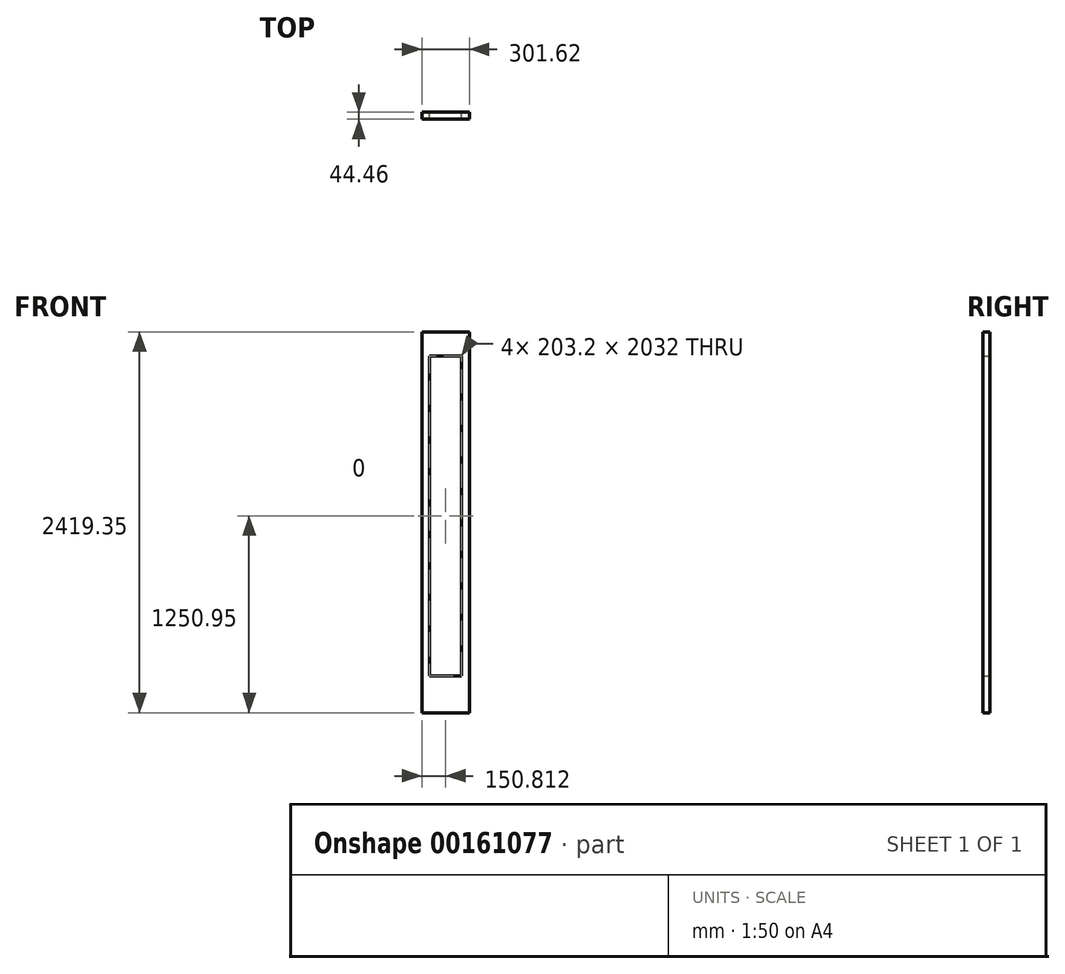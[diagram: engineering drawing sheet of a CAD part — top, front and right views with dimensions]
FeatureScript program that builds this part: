
annotation { "Feature Type Name" : "Feature", "Feature Type Description" : "" }
export const myFeature = defineFeature(function(context is Context, id is Id, definition is map)
    precondition{}
    {
        {
            var Q0;
            Q0=qCreatedBy(makeId("Front.planeOp"),FACE);
            var sketch = newSketch(context, id + "F0", { "sketchPlane" : qUnion([Q0])});
            skLineSegment(sketch, "E0.bottom", {"start": v(0, 0) * mm, "end": v(301.63, 0) * mm});
            skLineSegment(sketch, "E0.top", {"start": v(0, 2419.35) * mm, "end": v(301.62, 2419.35) * mm});
            skLineSegment(sketch, "E0.left", {"start": v(0, 0) * mm, "end": v(0, 2419.35) * mm});
            skLineSegment(sketch, "E0.right", {"start": v(301.63, 0) * mm, "end": v(301.62, 2419.35) * mm});
            skLineSegment(sketch, "E1.bottom", {"start": v(49.21, 2266.95) * mm, "end": v(252.41, 2266.95) * mm});
            skLineSegment(sketch, "E1.top", {"start": v(49.21, 234.95) * mm, "end": v(252.41, 234.95) * mm});
            skLineSegment(sketch, "E1.left", {"start": v(49.21, 2266.95) * mm, "end": v(49.21, 234.95) * mm});
            skLineSegment(sketch, "E1.right", {"start": v(252.41, 2266.95) * mm, "end": v(252.41, 234.95) * mm});
            skSolve(sketch);
        }
        {
            var Q0;
            Q0=qSketchRegion(id+"F0",true);
            extrude(context, id + "F1", {"entities" : qUnion([Q0]), "depth" : 22.22 * mm, "hasSecondDirection" : true, "secondDirectionOppositeDirection" : true, "secondDirectionDepth" : 22.22 * mm});
        }
    });
